# Revit family: WT22
name_source: partatom
category: Lighting Fixtures
revit_build: Autodesk Revit Architecture 2012 (Build: 20110309_2315(x64)
units: mm (PartAtom-declared; Revit-internal decimal feet)

## types (3) — shared parameters
Color Filter = 16777215
Default Elevation = 48"
Description = Wet Location Lensed Troffer.
Dimming Lamp Color Temperature Shift = <None>
Finish = White
Finish2 = White
Lamp = F32T8
Length = 24"
Manufacturer = Columbia Lighting
Manufacturer Fax = (866)-898-1065
Model = WT22
Opal lens = Etched Glass
Product Documentation Link = http://www.columbialighting.com
Product Page URL = http://www.columbialighting.com
Tilt Angle = -90.00°
URL = http://www.columbialighting.com
Wattage Comments = 87 W
Width = 24"

## per-type parameters (varying)
| type | Emit from Line Length | Photometric Web File |
| WT22- 2 Lamp | 20" | 13746.IES |
| WT22- 3 Lamp | 24" | 13747.IES |
| WT22- 4 Lamp | 24" | 13747.IES |

## geometry (parser evidence)
native form markers: Sweep x3
no freeform markers — native parametric forms only
